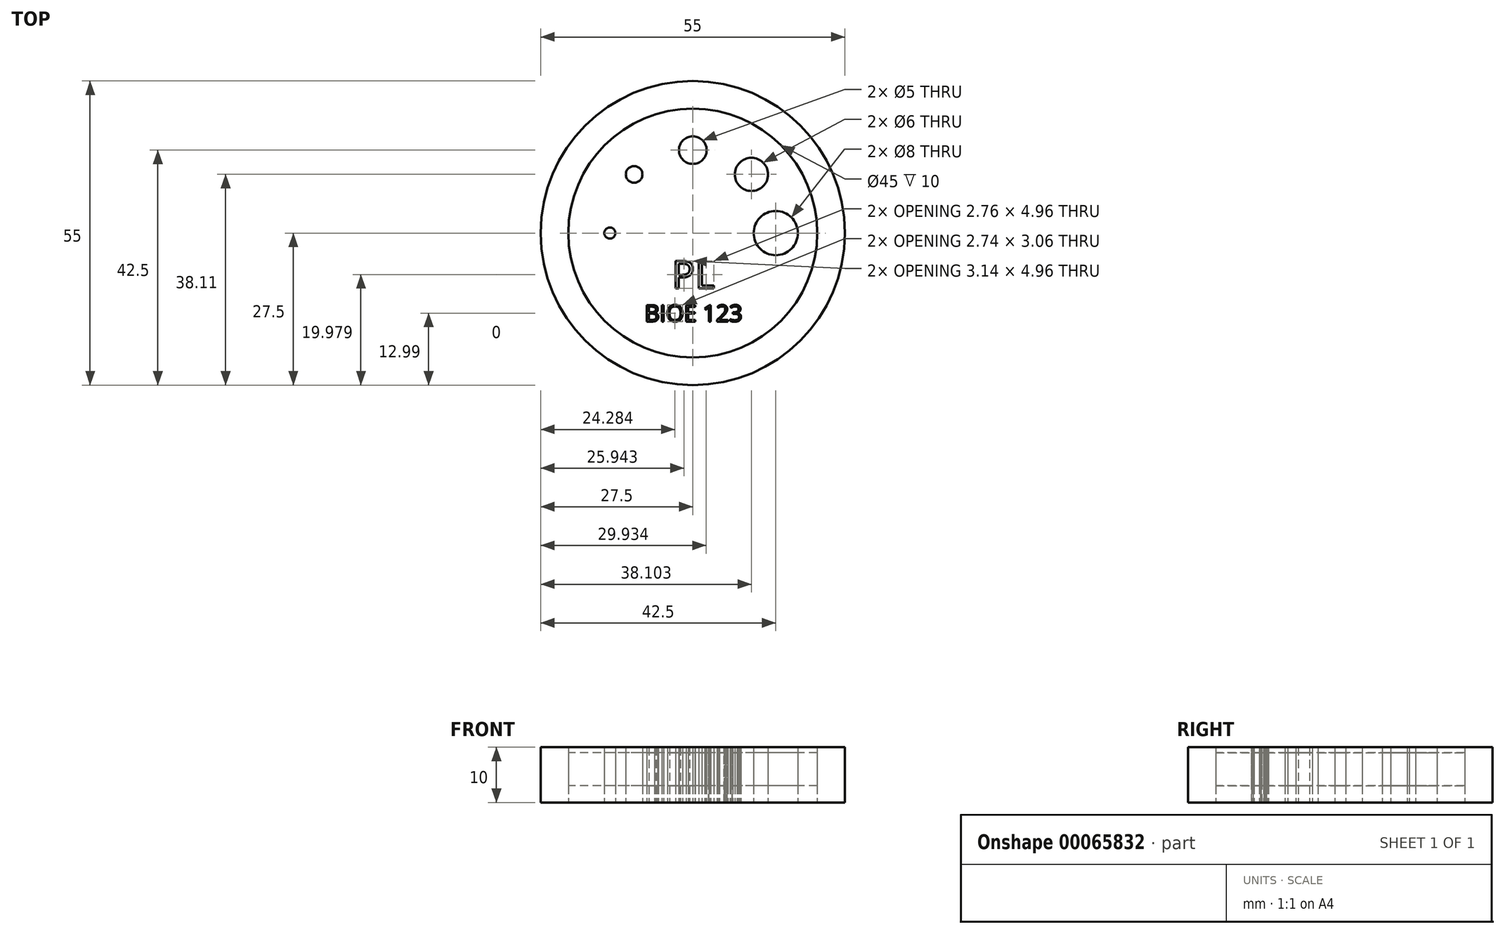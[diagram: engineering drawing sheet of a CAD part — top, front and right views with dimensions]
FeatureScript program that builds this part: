
annotation { "Feature Type Name" : "Feature", "Feature Type Description" : "" }
export const myFeature = defineFeature(function(context is Context, id is Id, definition is map)
    precondition{}
    {
        {
            var Q0;
            Q0=qCreatedBy(makeId("Top.planeOp"),FACE);
            var sketch = newSketch(context, id + "F0", { "sketchPlane" : qUnion([Q0])});
            skCircle(sketch, "E0", {"center": v(0, 0) * mm, "radius": 27.5 * mm});
            skCircle(sketch, "E1", {"center": v(0, 0) * mm, "radius": 22.5 * mm});
            skCircle(sketch, "E2", {"center": v(-15, 0) * mm, "radius": 1 * mm});
            skCircle(sketch, "E3", {"center": v(-10.6, 10.6) * mm, "radius": 1.5 * mm});
            skCircle(sketch, "E4", {"center": v(0, 15) * mm, "radius": 2.5 * mm});
            skCircle(sketch, "E5", {"center": v(10.6, 10.6) * mm, "radius": 3 * mm});
            skCircle(sketch, "E6", {"center": v(15, 0) * mm, "radius": 4 * mm});
            skText(sketch, "E7", { "text": "BIOE 123", "fontName": "OpenSans-Regular.ttf"});
            skText(sketch, "E8", { "text": "PL", "fontName": "OpenSans-Regular.ttf"});
            const initialGuessF0  = {"E7": [-0.0087, -0.016, 1, 0, 0.003], "E8": [-0.00381, -0.01, 1, 0, 0.005]};
            skSetInitialGuess(sketch, initialGuessF0);
            skSolve(sketch);
        }
        {
            var Q0;
            Q0=makeQuery(id+"F0.imprint","IMPRINT",FACE,{"disambiguationData":[TD([[makeQuery(id+"F0.imprint","IMPRINT",EDGE,{"derivedFrom":sQuery(id+"F0.wireOp",EDGE,"E7.sketch_text.stroke-0")}),-1.0]])]});
            var Q1;
            Q1=makeQuery(id+"F0.imprint","IMPRINT",FACE,{"disambiguationData":[TD([[makeQuery(id+"F0.imprint","IMPRINT",EDGE,{"derivedFrom":sQuery(id+"F0.wireOp",EDGE,"E7.sketch_text.stroke-25")}),-1.0]])]});
            var Q2;
            Q2=makeQuery(id+"F0.imprint","IMPRINT",FACE,{"disambiguationData":[TD([[makeQuery(id+"F0.imprint","IMPRINT",EDGE,{"derivedFrom":sQuery(id+"F0.wireOp",EDGE,"E7.sketch_text.stroke-29")}),-1.0]])]});
            var Q3;
            Q3=makeQuery(id+"F0.imprint","IMPRINT",FACE,{"disambiguationData":[TD([[makeQuery(id+"F0.imprint","IMPRINT",EDGE,{"derivedFrom":sQuery(id+"F0.wireOp",EDGE,"E0")}),1.0]])]});
            var Q4;
            Q4=makeQuery(id+"F0.imprint","IMPRINT",FACE,{"disambiguationData":[TD([[makeQuery(id+"F0.imprint","IMPRINT",EDGE,{"derivedFrom":sQuery(id+"F0.wireOp",EDGE,"E7.sketch_text.stroke-45")}),-1.0]])]});
            var Q5;
            Q5=makeQuery(id+"F0.imprint","IMPRINT",FACE,{"disambiguationData":[TD([[makeQuery(id+"F0.imprint","IMPRINT",EDGE,{"derivedFrom":sQuery(id+"F0.wireOp",EDGE,"E7.sketch_text.stroke-57")}),-1.0]])]});
            var Q6;
            Q6=makeQuery(id+"F0.imprint","IMPRINT",FACE,{"disambiguationData":[TD([[makeQuery(id+"F0.imprint","IMPRINT",EDGE,{"derivedFrom":sQuery(id+"F0.wireOp",EDGE,"E7.sketch_text.stroke-66")}),-1.0]])]});
            var Q7;
            Q7=makeQuery(id+"F0.imprint","IMPRINT",FACE,{"disambiguationData":[TD([[makeQuery(id+"F0.imprint","IMPRINT",EDGE,{"derivedFrom":sQuery(id+"F0.wireOp",EDGE,"E7.sketch_text.stroke-86")}),-1.0]])]});
            var Q8;
            Q8=makeQuery(id+"F0.imprint","IMPRINT",FACE,{"disambiguationData":[TD([[makeQuery(id+"F0.imprint","IMPRINT",EDGE,{"derivedFrom":sQuery(id+"F0.wireOp",EDGE,"E4")}),1.0]])]});
            var Q9;
            Q9=makeQuery(id+"F0.imprint","IMPRINT",FACE,{"disambiguationData":[TD([[makeQuery(id+"F0.imprint","IMPRINT",EDGE,{"derivedFrom":sQuery(id+"F0.wireOp",EDGE,"E3")}),1.0]])]});
            var Q10;
            Q10=makeQuery(id+"F0.imprint","IMPRINT",FACE,{"disambiguationData":[TD([[makeQuery(id+"F0.imprint","IMPRINT",EDGE,{"derivedFrom":sQuery(id+"F0.wireOp",EDGE,"E5")}),1.0]])]});
            var Q11;
            Q11=makeQuery(id+"F0.imprint","IMPRINT",FACE,{"disambiguationData":[TD([[makeQuery(id+"F0.imprint","IMPRINT",EDGE,{"derivedFrom":sQuery(id+"F0.wireOp",EDGE,"E6")}),1.0]])]});
            var Q12;
            Q12=makeQuery(id+"F0.imprint","IMPRINT",FACE,{"disambiguationData":[TD([[makeQuery(id+"F0.imprint","IMPRINT",EDGE,{"derivedFrom":sQuery(id+"F0.wireOp",EDGE,"E2")}),1.0]])]});
            var Q13;
            Q13=makeQuery(id+"F0.imprint","IMPRINT",FACE,{"disambiguationData":[TD([[makeQuery(id+"F0.imprint","IMPRINT",EDGE,{"derivedFrom":sQuery(id+"F0.wireOp",EDGE,"E8.sketch_text.stroke-0")}),-1.0]])]});
            var Q14;
            Q14=makeQuery(id+"F0.imprint","IMPRINT",FACE,{"disambiguationData":[TD([[makeQuery(id+"F0.imprint","IMPRINT",EDGE,{"derivedFrom":sQuery(id+"F0.wireOp",EDGE,"E8.sketch_text.stroke-15")}),-1.0]])]});
            extrude(context, id + "F1", {"entities" : qUnion([Q0, Q1, Q2, Q3, Q4, Q5, Q6, Q7, Q8, Q9, Q10, Q11, Q12, Q13, Q14]), "depth" : 10 * mm});
        }
        {
            var Q0;
            Q0=makeQuery(id+"F0.imprint","IMPRINT",FACE,{"disambiguationData":[TD([[makeQuery(id+"F0.imprint","IMPRINT",EDGE,{"derivedFrom":sQuery(id+"F0.wireOp",EDGE,"E1")}),1.0]])]});
            var Q1;
            Q1=makeQuery(id+"F0.imprint","IMPRINT",FACE,{"disambiguationData":[TD([[makeQuery(id+"F0.imprint","IMPRINT",EDGE,{"derivedFrom":sQuery(id+"F0.wireOp",EDGE,"E8.sketch_text.stroke-8")}),1.0]])]});
            var Q2;
            Q2=makeQuery(id+"F0.imprint","IMPRINT",FACE,{"disambiguationData":[TD([[makeQuery(id+"F0.imprint","IMPRINT",EDGE,{"derivedFrom":sQuery(id+"F0.wireOp",EDGE,"E7.sketch_text.stroke-37")}),1.0]])]});
            var Q3;
            Q3=makeQuery(id+"F0.imprint","IMPRINT",FACE,{"disambiguationData":[TD([[makeQuery(id+"F0.imprint","IMPRINT",EDGE,{"derivedFrom":sQuery(id+"F0.wireOp",EDGE,"E7.sketch_text.stroke-11")}),1.0]])]});
            var Q4;
            Q4=makeQuery(id+"F0.imprint","IMPRINT",FACE,{"disambiguationData":[TD([[makeQuery(id+"F0.imprint","IMPRINT",EDGE,{"derivedFrom":sQuery(id+"F0.wireOp",EDGE,"E7.sketch_text.stroke-18")}),1.0]])]});
            extrude(context, id + "F2", {"entities" : qUnion([Q0, Q1, Q2, Q3, Q4]), "depth" : 3 * mm});
        }
        {
            var Q0;
            Q0=qCreatedBy(makeId("Top.planeOp"),FACE);
            cPlane(context, id + "F3", {"entities" : qUnion([Q0]), "cplaneType" : CPlaneType.OFFSET, "offset" : 3 * mm, "width" : 152.4 * mm, "height" : 152.4 * mm});
        }
        {
            var Q0;
            Q0=qCreatedBy(id+"F3.planeOp",FACE);
            var sketch = newSketch(context, id + "F4", { "sketchPlane" : qUnion([Q0])});
            skCircle(sketch, "E9", {"center": v(0, 0) * mm, "radius": 22.5 * mm});
            skCircle(sketch, "E10", {"center": v(-15, 0) * mm, "radius": 1 * mm});
            skCircle(sketch, "E11", {"center": v(-10.6, 10.6) * mm, "radius": 1.5 * mm});
            skCircle(sketch, "E12", {"center": v(15, 0) * mm, "radius": 4 * mm});
            skCircle(sketch, "E13", {"center": v(10.6, 10.6) * mm, "radius": 3 * mm});
            skCircle(sketch, "E14", {"center": v(0, 15) * mm, "radius": 2.5 * mm});
            skText(sketch, "E15", { "text": "PL", "fontName": "OpenSans-Regular.ttf"});
            skText(sketch, "E16", { "text": "BIOE 123", "fontName": "OpenSans-Regular.ttf"});
            const initialGuessF4  = {"E15": [-0.00381, -0.01, 1, 0, 0.005], "E16": [-0.0087, -0.016, 1, 0, 0.003]};
            skSetInitialGuess(sketch, initialGuessF4);
            skSolve(sketch);
        }
        {
            var Q0;
            Q0=makeQuery(id+"F4.imprint","IMPRINT",FACE,{"disambiguationData":[TD([[makeQuery(id+"F4.imprint","IMPRINT",EDGE,{"derivedFrom":sQuery(id+"F4.wireOp",EDGE,"E9")}),1.0]])]});
            extrude(context, id + "F5", {"entities" : qUnion([Q0]), "depth" : 6 * mm});
        }
    });
